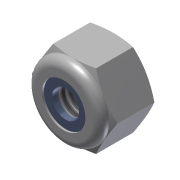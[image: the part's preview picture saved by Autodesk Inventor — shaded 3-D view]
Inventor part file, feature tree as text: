
AUTODESK INVENTOR PART (.ipt)
format: ipt  version: 2013 (Build 170138000, 138)  size: 183,296 bytes
history: native  units: in
note: dims shown in document units (in); Inventor stores cm internally (conversion verified against a paired STEP export)
features: sketch x5, extrude x2, revolve x2, projected_geometry x2, hole x1
ambient origin geometry x8: Origin, YZ Plane, XZ Plane, XY Plane, X Axis, Y Axis, Z Axis, Center Point
bodies: Solid1 (feature_tree)
feature tree (12):
  extrude  "Extrusion1"  Depth=0.195in TaperAngle=0.0deg
  revolve  "Revolution1"  [1 undecoded]
  revolve  "Revolution2"  Angle=90.0deg
  hole  "Hole1"  [1 undecoded]
  extrude  "Extrusion2"  Depth=0.027in
  sketch  "Sketch1"  dims[d0=0.3438in d1=0.195in d2=0.0in]
  sketch  "Sketch2"  dims[d5=0.039in d6=0.039in]
  sketch  "Sketch3"  dims[d7=0.133in d8=90.0deg]
  sketch  "Sketch4"  dims[d9=0.027in d10=0.012in]
  sketch  "Sketch5"  dims[d11=0.012in d12=0.027in d13=90.0deg d14=0.13in d15=0.75in d16=0.201in d17=0.009in d18=0.5635in d19=1.0in d20=0.8108in d21=0.125in d24=0.027in d25=0.0in]
  projected_geometry  "Project Cut Edges1"
  projected_geometry  "Project Cut Edges2"
note: 2 required parameter values undecoded (feature->parameter linkage not recoverable at this tier; creation-order binding heuristic only, values carry confidence <= 0.55)